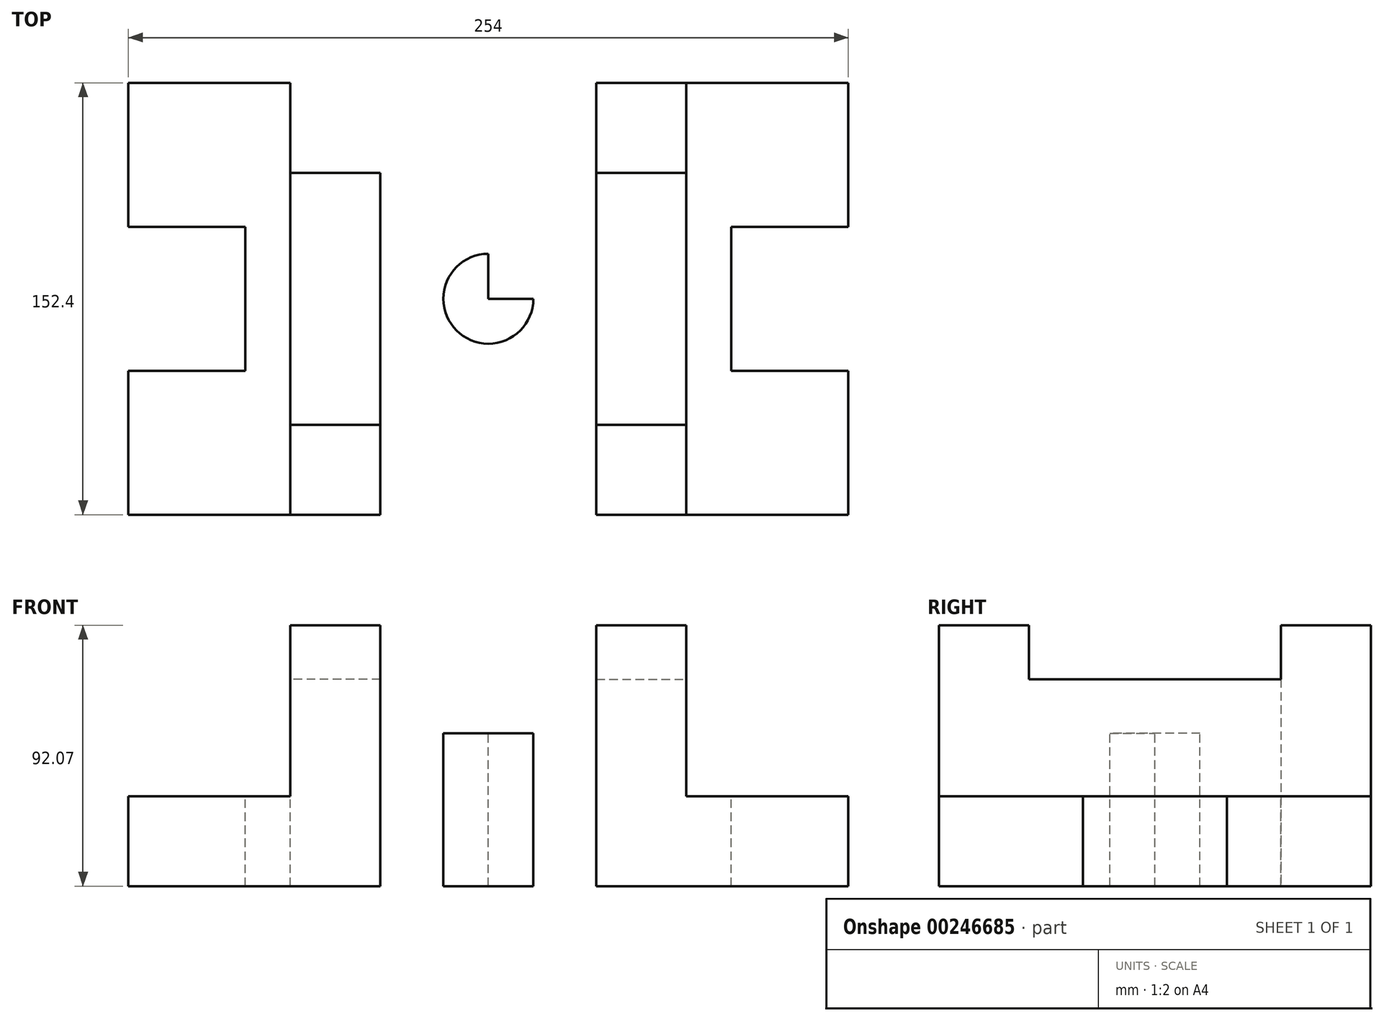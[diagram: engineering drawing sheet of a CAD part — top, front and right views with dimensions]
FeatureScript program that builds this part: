
annotation { "Feature Type Name" : "Feature", "Feature Type Description" : "" }
export const myFeature = defineFeature(function(context is Context, id is Id, definition is map)
    precondition{}
    {
        {
            var Q0;
            Q0=qCreatedBy(makeId("Top.planeOp"),FACE);
            var sketch = newSketch(context, id + "F0", { "sketchPlane" : qUnion([Q0])});
            skLineSegment(sketch, "E0", {"start": v(-142.94, -56.17) * mm, "end": v(111.06, -56.17) * mm});
            skLineSegment(sketch, "E1", {"start": v(-142.94, -56.17) * mm, "end": v(-142.94, -5.37) * mm});
            skLineSegment(sketch, "E2", {"start": v(-142.94, -5.37) * mm, "end": v(-101.67, -5.37) * mm});
            skLineSegment(sketch, "E3", {"start": v(-101.67, -5.37) * mm, "end": v(-101.67, 45.43) * mm});
            skLineSegment(sketch, "E4", {"start": v(-101.67, 45.43) * mm, "end": v(-142.94, 45.43) * mm});
            skLineSegment(sketch, "E5", {"start": v(-142.94, 45.43) * mm, "end": v(-142.94, 96.23) * mm});
            skLineSegment(sketch, "E6", {"start": v(-142.94, 96.23) * mm, "end": v(111.06, 96.23) * mm});
            skLineSegment(sketch, "E7", {"start": v(111.06, -56.17) * mm, "end": v(111.06, -5.37) * mm});
            skLineSegment(sketch, "E8", {"start": v(111.06, -5.37) * mm, "end": v(69.78, -5.37) * mm});
            skLineSegment(sketch, "E9", {"start": v(69.78, -5.37) * mm, "end": v(69.78, 45.43) * mm});
            skLineSegment(sketch, "E10", {"start": v(69.78, 45.43) * mm, "end": v(111.06, 45.43) * mm});
            skLineSegment(sketch, "E11", {"start": v(111.06, 45.43) * mm, "end": v(111.06, 96.23) * mm});
            skLineSegment(sketch, "E12", {"start": v(111.06, 96.23) * mm, "end": v(53.9, 96.23) * mm});
            skLineSegment(sketch, "E13", {"start": v(111.06, -56.17) * mm, "end": v(53.9, -56.17) * mm});
            skLineSegment(sketch, "E14", {"start": v(-142.94, 96.23) * mm, "end": v(-85.8, 96.23) * mm});
            skLineSegment(sketch, "E15", {"start": v(-142.94, -56.17) * mm, "end": v(-85.8, -56.17) * mm});
            skLineSegment(sketch, "E16", {"start": v(-85.8, -56.17) * mm, "end": v(-85.8, 96.23) * mm});
            skLineSegment(sketch, "E17", {"start": v(53.9, 96.23) * mm, "end": v(53.9, -56.17) * mm});
            skLineSegment(sketch, "E18", {"start": v(-85.8, 96.23) * mm, "end": v(-54.04, 96.23) * mm});
            skLineSegment(sketch, "E19", {"start": v(-54.04, 96.23) * mm, "end": v(-54.04, 64.48) * mm});
            skLineSegment(sketch, "E20", {"start": v(-54.04, 64.48) * mm, "end": v(-85.8, 64.48) * mm});
            skLineSegment(sketch, "E21", {"start": v(-85.8, -56.17) * mm, "end": v(-85.8, 20.03) * mm});
            skLineSegment(sketch, "E22", {"start": v(-85.8, 20.03) * mm, "end": v(53.9, 20.03) * mm});
            skLineSegment(sketch, "E23.MirrorCS", {"start": v(-54.04, -24.42) * mm, "end": v(-85.8, -24.42) * mm});
            skLineSegment(sketch, "E24.MirrorCS", {"start": v(-54.04, -56.17) * mm, "end": v(-54.04, -24.42) * mm});
            skLineSegment(sketch, "E25.MirrorCS", {"start": v(-85.8, -56.17) * mm, "end": v(-54.04, -56.17) * mm});
            skLineSegment(sketch, "E26", {"start": v(-54.04, 96.23) * mm, "end": v(-15.94, 96.23) * mm});
            skLineSegment(sketch, "E27", {"start": v(-15.94, 96.23) * mm, "end": v(-15.94, -56.17) * mm});
            skLineSegment(sketch, "E28.MirrorCS", {"start": v(22.16, 64.48) * mm, "end": v(53.9, 64.48) * mm});
            skLineSegment(sketch, "E29.MirrorCS", {"start": v(22.16, 96.23) * mm, "end": v(22.16, 64.48) * mm});
            skLineSegment(sketch, "E30.MirrorCS", {"start": v(53.9, 96.23) * mm, "end": v(22.16, 96.23) * mm});
            skLineSegment(sketch, "E31.MirrorCS", {"start": v(22.16, -24.42) * mm, "end": v(53.9, -24.42) * mm});
            skLineSegment(sketch, "E32.MirrorCS", {"start": v(22.16, -56.17) * mm, "end": v(22.16, -24.42) * mm});
            skLineSegment(sketch, "E33.MirrorCS", {"start": v(53.9, -56.17) * mm, "end": v(22.16, -56.17) * mm});
            skLineSegment(sketch, "E34", {"start": v(-54.04, 64.48) * mm, "end": v(-54.04, -24.42) * mm});
            skLineSegment(sketch, "E35", {"start": v(22.16, -24.42) * mm, "end": v(22.16, 64.48) * mm});
            skSolve(sketch);
        }
        {
            var Q0;
            Q0=makeQuery(id+"F0.imprint","IMPRINT",FACE,{"disambiguationData":[TD([[makeQuery(id+"F0.imprint","IMPRINT",EDGE,{"derivedFrom":sQuery(id+"F0.wireOp",EDGE,"E1")}),-1.0]])]});
            var Q1;
            {var subQ2=sQuery(id+"F0.wireOp",EDGE,"E23.MirrorCS");Q1=makeQuery(id+"F0.imprint","IMPRINT",FACE,{"disambiguationData":[TD([[makeQuery(id+"F0.imprint","IMPRINT",EDGE,{"derivedFrom":subQ2}),1.0]])]});}
            var Q2;
            {var subQ3=sQuery(id+"F0.wireOp",EDGE,"E23.MirrorCS");Q2=makeQuery(id+"F0.imprint","IMPRINT",FACE,{"disambiguationData":[TD([[makeQuery(id+"F0.imprint","IMPRINT",EDGE,{"derivedFrom":subQ3}),-1.0]])]});}
            var Q3;
            {var subQ3=sQuery(id+"F0.wireOp",EDGE,"E20");Q3=makeQuery(id+"F0.imprint","IMPRINT",FACE,{"disambiguationData":[TD([[makeQuery(id+"F0.imprint","IMPRINT",EDGE,{"derivedFrom":subQ3}),1.0]])]});}
            var Q4;
            {var subQ0=sQuery(id+"F0.wireOp",EDGE,"E18");Q4=makeQuery(id+"F0.imprint","IMPRINT",FACE,{"disambiguationData":[TD([[makeQuery(id+"F0.imprint","IMPRINT",EDGE,{"derivedFrom":subQ0}),-1.0]])]});}
            var Q5;
            {var subQ7=sQuery(id+"F0.wireOp",EDGE,"E24.MirrorCS");Q5=makeQuery(id+"F0.imprint","IMPRINT",FACE,{"disambiguationData":[TD([[makeQuery(id+"F0.imprint","IMPRINT",EDGE,{"derivedFrom":subQ7}),-1.0]])]});}
            var Q6;
            {var subQ6=sQuery(id+"F0.wireOp",EDGE,"E19");Q6=makeQuery(id+"F0.imprint","IMPRINT",FACE,{"disambiguationData":[TD([[makeQuery(id+"F0.imprint","IMPRINT",EDGE,{"derivedFrom":subQ6}),1.0]])]});}
            var Q7;
            {var subQ5=sQuery(id+"F0.wireOp",EDGE,"E32.MirrorCS");Q7=makeQuery(id+"F0.imprint","IMPRINT",FACE,{"disambiguationData":[TD([[makeQuery(id+"F0.imprint","IMPRINT",EDGE,{"derivedFrom":subQ5}),1.0]])]});}
            var Q8;
            {var subQ2=sQuery(id+"F0.wireOp",EDGE,"E31.MirrorCS");Q8=makeQuery(id+"F0.imprint","IMPRINT",FACE,{"disambiguationData":[TD([[makeQuery(id+"F0.imprint","IMPRINT",EDGE,{"derivedFrom":subQ2}),-1.0]])]});}
            var Q9;
            Q9=makeQuery(id+"F0.imprint","IMPRINT",FACE,{"disambiguationData":[TD([[makeQuery(id+"F0.imprint","IMPRINT",EDGE,{"derivedFrom":sQuery(id+"F0.wireOp",EDGE,"E7")}),1.0]])]});
            var Q10;
            {var subQ1=sQuery(id+"F0.wireOp",EDGE,"E6");Q10=makeQuery(id+"F0.imprint","IMPRINT",FACE,{"disambiguationData":[TD([[makeQuery(id+"F0.imprint","IMPRINT",EDGE,{"derivedFrom":subQ1}),-1.0]])]});}
            var Q11;
            {var subQ2=sQuery(id+"F0.wireOp",EDGE,"E28.MirrorCS");Q11=makeQuery(id+"F0.imprint","IMPRINT",FACE,{"disambiguationData":[TD([[makeQuery(id+"F0.imprint","IMPRINT",EDGE,{"derivedFrom":subQ2}),1.0]])]});}
            var Q12;
            {var subQ3=sQuery(id+"F0.wireOp",EDGE,"E28.MirrorCS");Q12=makeQuery(id+"F0.imprint","IMPRINT",FACE,{"disambiguationData":[TD([[makeQuery(id+"F0.imprint","IMPRINT",EDGE,{"derivedFrom":subQ3}),-1.0]])]});}
            var Q13;
            {var subQ3=sQuery(id+"F0.wireOp",EDGE,"E31.MirrorCS");Q13=makeQuery(id+"F0.imprint","IMPRINT",FACE,{"disambiguationData":[TD([[makeQuery(id+"F0.imprint","IMPRINT",EDGE,{"derivedFrom":subQ3}),1.0]])]});}
            extrude(context, id + "F1", {"entities" : qUnion([Q0, Q1, Q2, Q3, Q4, Q5, Q6, Q7, Q8, Q9, Q10, Q11, Q12, Q13]), "oppositeDirection" : true, "depth" : 31.75 * mm});
        }
        {
            var Q0;
            {var subQ0=sQuery(id+"F0.wireOp",EDGE,"E18");Q0=makeQuery(id+"F0.imprint","IMPRINT",FACE,{"disambiguationData":[TD([[makeQuery(id+"F0.imprint","IMPRINT",EDGE,{"derivedFrom":subQ0}),-1.0]])]});}
            var Q1;
            {var subQ2=sQuery(id+"F0.wireOp",EDGE,"E23.MirrorCS");Q1=makeQuery(id+"F0.imprint","IMPRINT",FACE,{"disambiguationData":[TD([[makeQuery(id+"F0.imprint","IMPRINT",EDGE,{"derivedFrom":subQ2}),1.0]])]});}
            var Q2;
            {var subQ2=sQuery(id+"F0.wireOp",EDGE,"E28.MirrorCS");Q2=makeQuery(id+"F0.imprint","IMPRINT",FACE,{"disambiguationData":[TD([[makeQuery(id+"F0.imprint","IMPRINT",EDGE,{"derivedFrom":subQ2}),1.0]])]});}
            var Q3;
            {var subQ2=sQuery(id+"F0.wireOp",EDGE,"E31.MirrorCS");Q3=makeQuery(id+"F0.imprint","IMPRINT",FACE,{"disambiguationData":[TD([[makeQuery(id+"F0.imprint","IMPRINT",EDGE,{"derivedFrom":subQ2}),-1.0]])]});}
            extrude(context, id + "F2", {"entities" : qUnion([Q0, Q1, Q2, Q3]), "operationType" : NewBodyOperationType.ADD, "depth" : 60.32 * mm});
        }
        {
            var Q0;
            {var subQ3=sQuery(id+"F0.wireOp",EDGE,"E23.MirrorCS");Q0=makeQuery(id+"F0.imprint","IMPRINT",FACE,{"disambiguationData":[TD([[makeQuery(id+"F0.imprint","IMPRINT",EDGE,{"derivedFrom":subQ3}),-1.0]])]});}
            var Q1;
            {var subQ3=sQuery(id+"F0.wireOp",EDGE,"E20");Q1=makeQuery(id+"F0.imprint","IMPRINT",FACE,{"disambiguationData":[TD([[makeQuery(id+"F0.imprint","IMPRINT",EDGE,{"derivedFrom":subQ3}),1.0]])]});}
            var Q2;
            {var subQ3=sQuery(id+"F0.wireOp",EDGE,"E28.MirrorCS");Q2=makeQuery(id+"F0.imprint","IMPRINT",FACE,{"disambiguationData":[TD([[makeQuery(id+"F0.imprint","IMPRINT",EDGE,{"derivedFrom":subQ3}),-1.0]])]});}
            var Q3;
            {var subQ3=sQuery(id+"F0.wireOp",EDGE,"E31.MirrorCS");Q3=makeQuery(id+"F0.imprint","IMPRINT",FACE,{"disambiguationData":[TD([[makeQuery(id+"F0.imprint","IMPRINT",EDGE,{"derivedFrom":subQ3}),1.0]])]});}
            extrude(context, id + "F3", {"entities" : qUnion([Q0, Q1, Q2, Q3]), "operationType" : NewBodyOperationType.ADD, "depth" : 41.27 * mm});
        }
        {
            var Q0;
            {var subQ6=sQuery(id+"F0.wireOp",EDGE,"E19");Q0=makeQuery(id+"F0.imprint","IMPRINT",FACE,{"disambiguationData":[TD([[makeQuery(id+"F0.imprint","IMPRINT",EDGE,{"derivedFrom":subQ6}),1.0]])]});}
            var Q1;
            {var subQ7=sQuery(id+"F0.wireOp",EDGE,"E24.MirrorCS");Q1=makeQuery(id+"F0.imprint","IMPRINT",FACE,{"disambiguationData":[TD([[makeQuery(id+"F0.imprint","IMPRINT",EDGE,{"derivedFrom":subQ7}),-1.0]])]});}
            var Q2;
            {var subQ1=sQuery(id+"F0.wireOp",EDGE,"E6");Q2=makeQuery(id+"F0.imprint","IMPRINT",FACE,{"disambiguationData":[TD([[makeQuery(id+"F0.imprint","IMPRINT",EDGE,{"derivedFrom":subQ1}),-1.0]])]});}
            var Q3;
            {var subQ5=sQuery(id+"F0.wireOp",EDGE,"E32.MirrorCS");Q3=makeQuery(id+"F0.imprint","IMPRINT",FACE,{"disambiguationData":[TD([[makeQuery(id+"F0.imprint","IMPRINT",EDGE,{"derivedFrom":subQ5}),1.0]])]});}
            extrude(context, id + "F4", {"entities" : qUnion([Q0, Q1, Q2, Q3]), "operationType" : NewBodyOperationType.ADD, "depth" : 22.22 * mm});
        }
        {
            var Q0;
            Q0=makeQuery(id+"F4.opExtrude","CAP_FACE",FACE,{"disambiguationData":[OSD([sQuery(id+"F0.wireOp",EDGE,"E0"),sQuery(id+"F0.wireOp",EDGE,"E6"),sQuery(id+"F0.wireOp",EDGE,"E19"),sQuery(id+"F0.wireOp",EDGE,"E24.MirrorCS"),sQuery(id+"F0.wireOp",EDGE,"E26"),sQuery(id+"F0.wireOp",EDGE,"E29.MirrorCS"),sQuery(id+"F0.wireOp",EDGE,"E32.MirrorCS"),sQuery(id+"F0.wireOp",EDGE,"E34"),sQuery(id+"F0.wireOp",EDGE,"E35")])],"isStart":false});
            var sketch = newSketch(context, id + "F5", { "sketchPlane" : qUnion([Q0])});
            skLineSegment(sketch, "E36", {"start": v(-54.04, 96.23) * mm, "end": v(-15.94, 96.23) * mm});
            skLineSegment(sketch, "E37.MirrorCS", {"start": v(-15.94, 96.23) * mm, "end": v(-15.94, 20.03) * mm});
            skCircle(sketch, "E38.MirrorC", {"center": v(-15.94, 20.03) * mm, "radius": 15.88 * mm});
            skPoint(sketch, "E39.end.orphan", {"position": v(-15.94, 172.43) * mm});
            skSolve(sketch);
        }
        {
            var Q0;
            Q0=makeQuery(id+"F5.imprint","IMPRINT",FACE,{"disambiguationData":[TD([[makeQuery(id+"F5.imprint","IMPRINT",EDGE,{"derivedFrom":sQuery(id+"F5.wireOp",EDGE,"E38.MirrorC")}),-1.0]])]});
            extrude(context, id + "F6", {"entities" : qUnion([Q0]), "operationType" : NewBodyOperationType.REMOVE, "endBound" : BoundingType.THROUGH_ALL, "oppositeDirection" : true, "depth" : 25.4 * mm});
        }
    });
